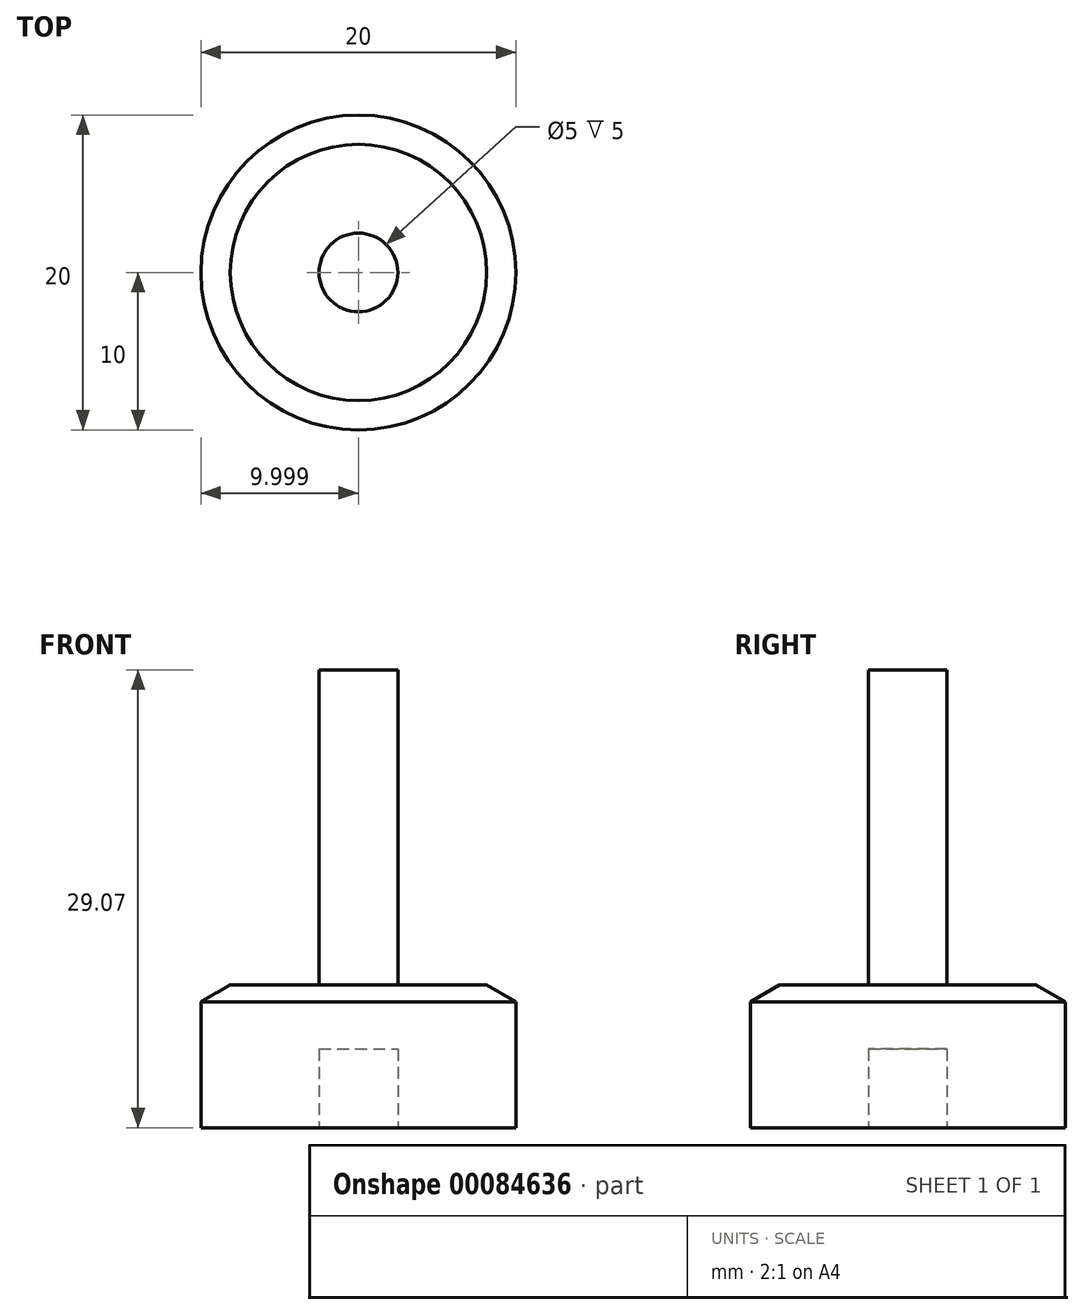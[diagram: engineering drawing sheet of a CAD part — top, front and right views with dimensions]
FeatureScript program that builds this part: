
annotation { "Feature Type Name" : "Feature", "Feature Type Description" : "" }
export const myFeature = defineFeature(function(context is Context, id is Id, definition is map)
    precondition{}
    {
        {
            var Q0;
            Q0=qCreatedBy(makeId("Front.planeOp"),FACE);
            var sketch = newSketch(context, id + "F0", { "sketchPlane" : qUnion([Q0])});
            skLineSegment(sketch, "E0.bottom", {"start": v(-30.55, 8) * mm, "end": v(-20.55, 8) * mm});
            skLineSegment(sketch, "E0.top", {"start": v(-30.55, 0) * mm, "end": v(-23.05, 0) * mm});
            skLineSegment(sketch, "E0.left", {"start": v(-30.55, 8) * mm, "end": v(-30.55, 0) * mm});
            skPoint(sketch, "E1", {"position": v(-20.55, 8) * mm});
            skPoint(sketch, "E2", {"position": v(-20.55, 0) * mm});
            skPoint(sketch, "E3", {"position": v(-20.55, 9.07) * mm});
            skLineSegment(sketch, "E4", {"start": v(-20.55, 8) * mm, "end": v(-20.55, 9.07) * mm});
            skLineSegment(sketch, "E5", {"start": v(-30.55, 8) * mm, "end": v(-28.7, 9.07) * mm});
            skLineSegment(sketch, "E6", {"start": v(-28.7, 9.07) * mm, "end": v(-20.55, 9.07) * mm});
            skLineSegment(sketch, "E7", {"start": v(-20.55, 8) * mm, "end": v(-20.55, 5) * mm});
            skPoint(sketch, "E0.right.end.orphan", {"position": v(-10.55, 0) * mm});
            skPoint(sketch, "E8.start.orphan", {"position": v(-10.55, 8) * mm});
            skLineSegment(sketch, "E9", {"start": v(-20.55, 9.07) * mm, "end": v(-20.55, 29.07) * mm});
            skLineSegment(sketch, "E10", {"start": v(-20.55, 29.07) * mm, "end": v(-23.05, 29.07) * mm});
            skLineSegment(sketch, "E11", {"start": v(-23.05, 29.07) * mm, "end": v(-23.05, 0) * mm});
            skPoint(sketch, "E12.start.orphan", {"position": v(-20.55, 4) * mm});
            skLineSegment(sketch, "E13", {"start": v(-20.55, 5) * mm, "end": v(-23.05, 5) * mm});
            skPoint(sketch, "E14", {"position": v(-20.55, 5) * mm});
            skSolve(sketch);
        }
        {
            var Q0;
            {var subQ0=sQuery(id+"F0.wireOp",EDGE,"E9");Q0=makeQuery(id+"F0.imprint","IMPRINT",FACE,{"disambiguationData":[TD([[makeQuery(id+"F0.imprint","IMPRINT",EDGE,{"derivedFrom":subQ0}),1.0]])]});}
            var Q1;
            {var subQ5=sQuery(id+"F0.wireOp",EDGE,"E0.top");Q1=makeQuery(id+"F0.imprint","IMPRINT",FACE,{"disambiguationData":[TD([[makeQuery(id+"F0.imprint","IMPRINT",EDGE,{"derivedFrom":subQ5}),1.0]])]});}
            var Q2;
            {var subQ0=sQuery(id+"F0.wireOp",EDGE,"E5");Q2=makeQuery(id+"F0.imprint","IMPRINT",FACE,{"disambiguationData":[TD([[makeQuery(id+"F0.imprint","IMPRINT",EDGE,{"derivedFrom":subQ0}),-1.0]])]});}
            var Q3;
            {var subQ0=sQuery(id+"F0.wireOp",EDGE,"E7");Q3=makeQuery(id+"F0.imprint","IMPRINT",FACE,{"disambiguationData":[TD([[makeQuery(id+"F0.imprint","IMPRINT",EDGE,{"derivedFrom":subQ0}),-1.0]])]});}
            var Q4;
            {var subQ0=sQuery(id+"F0.wireOp",EDGE,"E4");Q4=makeQuery(id+"F0.imprint","IMPRINT",FACE,{"disambiguationData":[TD([[makeQuery(id+"F0.imprint","IMPRINT",EDGE,{"derivedFrom":subQ0}),1.0]])]});}
            var Q5;
            Q5=sQuery(id+"F0.wireOp",EDGE,"E9");
            revolve(context, id + "F1", {"entities" : qUnion([Q0, Q1, Q2, Q3, Q4]), "axis" : qUnion([Q5]), "revolveType" : RevolveType.FULL});
        }
    });
